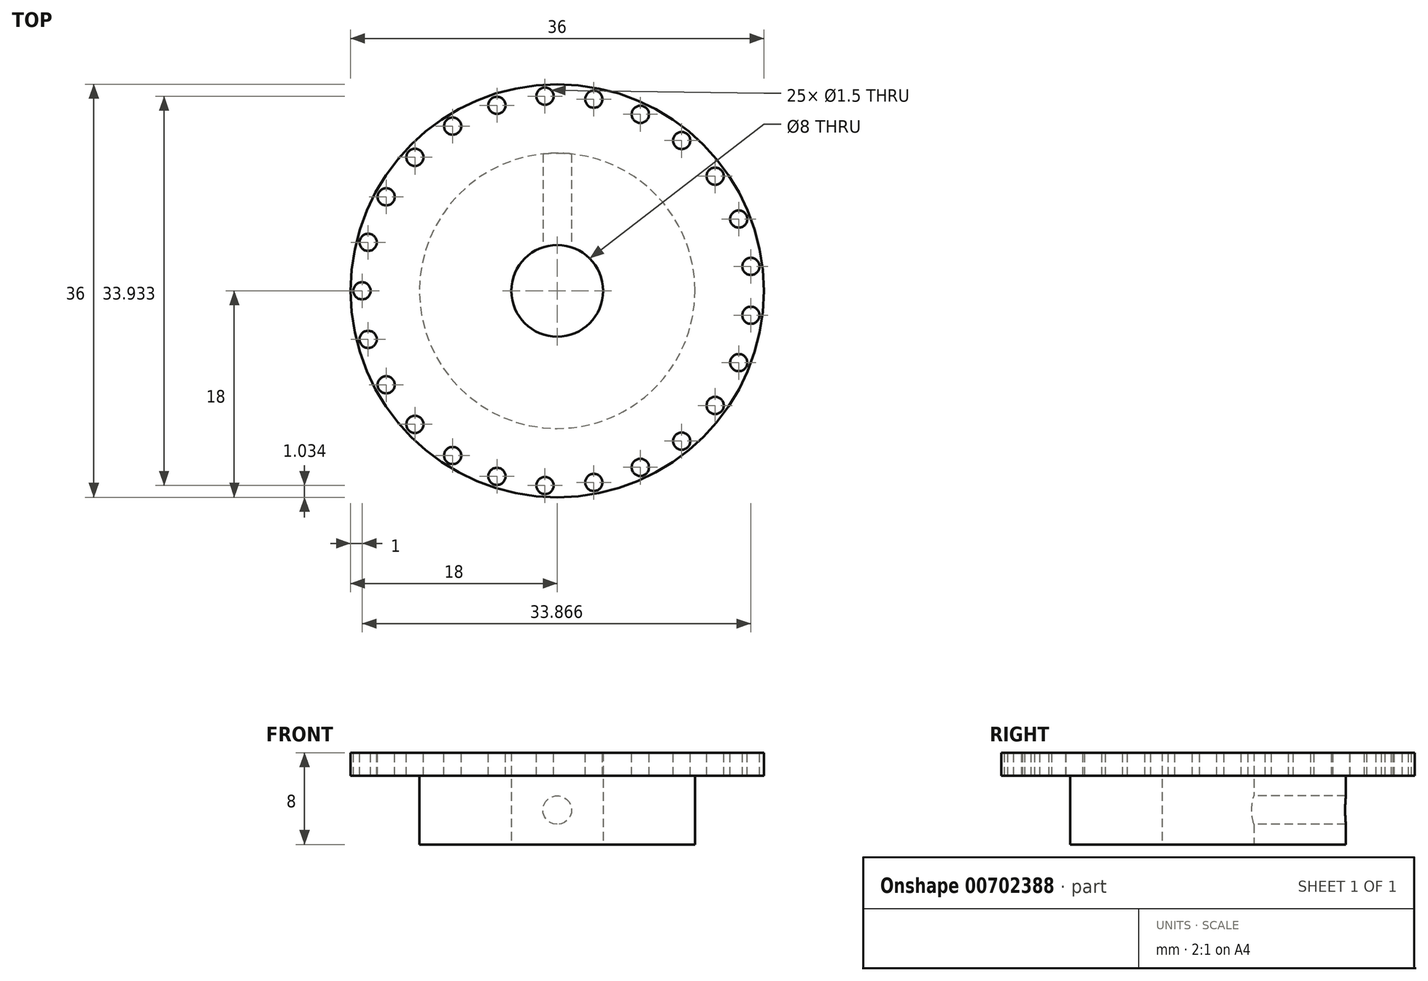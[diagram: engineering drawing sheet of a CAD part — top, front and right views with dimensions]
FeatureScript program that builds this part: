
annotation { "Feature Type Name" : "Feature", "Feature Type Description" : "" }
export const myFeature = defineFeature(function(context is Context, id is Id, definition is map)
    precondition{}
    {
        {
            var Q0;
            Q0=qCreatedBy(makeId("Top.planeOp"),FACE);
            var sketch = newSketch(context, id + "F0", { "sketchPlane" : qUnion([Q0])});
            skCircle(sketch, "E0", {"center": v(0, 0) * mm, "radius": 12 * mm});
            skSolve(sketch);
        }
        {
            var Q0;
            Q0 = qSketchRegion(id + "F0", true);
            extrude(context, id + "F1", {"entities" : qUnion([Q0]), "depth" : 6 * mm, "offsetDistance" : 25 * mm});
        }
        {
            var Q0;
            Q0=makeQuery(id+"F1.opExtrude","CAP_FACE",FACE,{"disambiguationData":[OSD([sQuery(id+"F0.wireOp",EDGE,"E0")])],"isStart":false});
            var sketch = newSketch(context, id + "F2", { "sketchPlane" : qUnion([Q0])});
            skCircle(sketch, "E1", {"center": v(0, 0) * mm, "radius": 18 * mm});
            skSolve(sketch);
        }
        {
            var Q0;
            Q0 = qSketchRegion(id + "F2", true);
            extrude(context, id + "F3", {"entities" : qUnion([Q0]), "operationType" : NewBodyOperationType.ADD, "depth" : 2 * mm, "offsetDistance" : 25 * mm});
        }
        {
            var Q0;
            Q0=makeQuery(id+"F3.opExtrude","CAP_FACE",FACE,{"disambiguationData":[OSD([sQuery(id+"F2.wireOp",EDGE,"E1")])],"isStart":false});
            var sketch = newSketch(context, id + "F4", { "sketchPlane" : qUnion([Q0])});
            skCircle(sketch, "E2", {"center": v(0, 0) * mm, "radius": 18 * mm});
            skCircle(sketch, "E3.0", {"center": v(0, 0) * mm, "radius": 17 * mm});
            skCircle(sketch, "E4", {"center": v(-17, 0) * mm, "radius": 0.75 * mm});
            skCircle(sketch, "E5.1.0", {"center": v(-16.47, -4.23) * mm, "radius": 0.75 * mm});
            skCircle(sketch, "E5.2.0", {"center": v(-14.9, -8.19) * mm, "radius": 0.75 * mm});
            skCircle(sketch, "E5.3.0", {"center": v(-12.4, -11.64) * mm, "radius": 0.75 * mm});
            skCircle(sketch, "E5.4.0", {"center": v(-9.1, -14.35) * mm, "radius": 0.75 * mm});
            skCircle(sketch, "E5.5.0", {"center": v(-5.25, -16.17) * mm, "radius": 0.75 * mm});
            skCircle(sketch, "E5.6.0", {"center": v(-1.07, -16.97) * mm, "radius": 0.75 * mm});
            skCircle(sketch, "E5.7.0", {"center": v(3.19, -16.7) * mm, "radius": 0.75 * mm});
            skCircle(sketch, "E5.8.0", {"center": v(7.24, -15.38) * mm, "radius": 0.75 * mm});
            skCircle(sketch, "E5.9.0", {"center": v(10.84, -13.1) * mm, "radius": 0.75 * mm});
            skCircle(sketch, "E5.10.0", {"center": v(13.75, -10) * mm, "radius": 0.75 * mm});
            skCircle(sketch, "E5.11.0", {"center": v(15.8, -6.26) * mm, "radius": 0.75 * mm});
            skCircle(sketch, "E5.12.0", {"center": v(16.87, -2.13) * mm, "radius": 0.75 * mm});
            skCircle(sketch, "E5.13.0", {"center": v(16.87, 2.13) * mm, "radius": 0.75 * mm});
            skCircle(sketch, "E5.14.0", {"center": v(15.8, 6.26) * mm, "radius": 0.75 * mm});
            skCircle(sketch, "E5.15.0", {"center": v(13.75, 10) * mm, "radius": 0.75 * mm});
            skCircle(sketch, "E5.16.0", {"center": v(10.84, 13.1) * mm, "radius": 0.75 * mm});
            skCircle(sketch, "E5.17.0", {"center": v(7.24, 15.38) * mm, "radius": 0.75 * mm});
            skCircle(sketch, "E5.18.0", {"center": v(3.19, 16.7) * mm, "radius": 0.75 * mm});
            skCircle(sketch, "E5.19.0", {"center": v(-1.07, 16.97) * mm, "radius": 0.75 * mm});
            skCircle(sketch, "E5.20.0", {"center": v(-5.25, 16.17) * mm, "radius": 0.75 * mm});
            skCircle(sketch, "E5.21.0", {"center": v(-9.1, 14.35) * mm, "radius": 0.75 * mm});
            skCircle(sketch, "E5.22.0", {"center": v(-12.4, 11.64) * mm, "radius": 0.75 * mm});
            skCircle(sketch, "E5.23.0", {"center": v(-14.9, 8.19) * mm, "radius": 0.75 * mm});
            skCircle(sketch, "E5.24.0", {"center": v(-16.47, 4.23) * mm, "radius": 0.75 * mm});
            skSolve(sketch);
        }
        {
            var Q0;
            Q0=sQuery(id+"F4.wireOp",VERTEX,"E4.center");
            var Q1;
            Q1=sQuery(id+"F4.wireOp",VERTEX,"E5.24.0.center");
            var Q2;
            Q2=sQuery(id+"F4.wireOp",VERTEX,"E5.23.0.center");
            var Q3;
            Q3=sQuery(id+"F4.wireOp",VERTEX,"E5.22.0.center");
            var Q4;
            Q4=sQuery(id+"F4.wireOp",VERTEX,"E5.21.0.center");
            var Q5;
            Q5=sQuery(id+"F4.wireOp",VERTEX,"E5.20.0.center");
            var Q6;
            Q6=sQuery(id+"F4.wireOp",VERTEX,"E5.19.0.center");
            var Q7;
            Q7=sQuery(id+"F4.wireOp",VERTEX,"E5.18.0.center");
            var Q8;
            Q8=sQuery(id+"F4.wireOp",VERTEX,"E5.17.0.center");
            var Q9;
            Q9=sQuery(id+"F4.wireOp",VERTEX,"E5.16.0.center");
            var Q10;
            Q10=sQuery(id+"F4.wireOp",VERTEX,"E5.15.0.center");
            var Q11;
            Q11=sQuery(id+"F4.wireOp",VERTEX,"E5.14.0.center");
            var Q12;
            Q12=sQuery(id+"F4.wireOp",VERTEX,"E5.1.0.center");
            var Q13;
            Q13=sQuery(id+"F4.wireOp",VERTEX,"E5.2.0.center");
            var Q14;
            Q14=sQuery(id+"F4.wireOp",VERTEX,"E5.3.0.center");
            var Q15;
            Q15=sQuery(id+"F4.wireOp",VERTEX,"E5.4.0.center");
            var Q16;
            Q16=sQuery(id+"F4.wireOp",VERTEX,"E5.5.0.center");
            var Q17;
            Q17=sQuery(id+"F4.wireOp",VERTEX,"E5.6.0.center");
            var Q18;
            Q18=sQuery(id+"F4.wireOp",VERTEX,"E5.7.0.center");
            var Q19;
            Q19=sQuery(id+"F4.wireOp",VERTEX,"E5.8.0.center");
            var Q20;
            Q20=sQuery(id+"F4.wireOp",VERTEX,"E5.9.0.center");
            var Q21;
            Q21=sQuery(id+"F4.wireOp",VERTEX,"E5.10.0.center");
            var Q22;
            Q22=sQuery(id+"F4.wireOp",VERTEX,"E5.11.0.center");
            var Q23;
            Q23=sQuery(id+"F4.wireOp",VERTEX,"E5.12.0.center");
            var Q24;
            Q24=sQuery(id+"F4.wireOp",VERTEX,"E5.13.0.center");
            var Q25;
            Q25=makeQuery(id+"F1.opExtrude","SWEPT_BODY",BODY,{"disambiguationData":[OSD([sQuery(id+"F0.wireOp",EDGE,"E0")])]});
            hole(context, id + "F5", {"style" : HoleStyle.SIMPLE, "endStyle" : HoleEndStyle.THROUGH, "holeDiameter" : 1.5 * mm, "majorDiameter" : 5 * mm, "isTappedThrough" : true, "tappedDepth" : 12 * mm, "tapClearance" : 3, "locations" : qUnion([Q0, Q1, Q2, Q3, Q4, Q5, Q6, Q7, Q8, Q9, Q10, Q11, Q12, Q13, Q14, Q15, Q16, Q17, Q18, Q19, Q20, Q21, Q22, Q23, Q24]), "scope" : qUnion([Q25])});
        }
        {
            var Q0;
            Q0=makeQuery(id+"F1.opExtrude","CAP_FACE",FACE,{"disambiguationData":[OSD([sQuery(id+"F0.wireOp",EDGE,"E0")])],"isStart":true});
            var sketch = newSketch(context, id + "F6", { "sketchPlane" : qUnion([Q0])});
            skCircle(sketch, "E6", {"center": v(0, 0) * mm, "radius": 4 * mm});
            skSolve(sketch);
        }
        {
            var Q0;
            Q0 = qSketchRegion(id + "F6", true);
            extrude(context, id + "F7", {"entities" : qUnion([Q0]), "operationType" : NewBodyOperationType.REMOVE, "endBound" : BoundingType.THROUGH_ALL, "oppositeDirection" : true, "depth" : 25 * mm, "offsetDistance" : 25 * mm});
        }
        {
            var Q0;
            Q0=qCreatedBy(makeId("Front.planeOp"),FACE);
            var sketch = newSketch(context, id + "F8", { "sketchPlane" : qUnion([Q0])});
            skLineSegment(sketch, "E7", {"start": v(0, 0) * mm, "end": v(0, 11.38) * mm});
            skLineSegment(sketch, "E8", {"start": v(-13.15, 0) * mm, "end": v(15.67, 0) * mm});
            skLineSegment(sketch, "E9.0", {"start": v(-13.15, 3) * mm, "end": v(15.67, 3) * mm});
            skCircle(sketch, "E10", {"center": v(0, 3) * mm, "radius": 1.55 * mm});
            skSolve(sketch);
        }
        {
            var Q0;
            Q0=sQuery(id+"F8.wireOp",VERTEX,"E10.center");
            var Q1;
            Q1=makeQuery(id+"F1.opExtrude","SWEPT_BODY",BODY,{"disambiguationData":[OSD([sQuery(id+"F0.wireOp",EDGE,"E0")])]});
            hole(context, id + "F9", {"style" : HoleStyle.SIMPLE, "endStyle" : HoleEndStyle.THROUGH, "standardTappedOrClearance" : lookupTablePath({ "standard" : "ISO", "engagement" : "75%", "pitch" : "0.5 mm", "size" : "M3", "type" : "Tapped" }), "standardBlindInLast" : lookupTablePath({ "standard" : "ISO", "engagement" : "75%", "pitch" : "0.5 mm", "size" : "M3", "type" : "Tapped" }), "holeDiameter" : 2.5 * mm, "majorDiameter" : 3 * mm, "showTappedDepth" : true, "isTappedThrough" : true, "tappedDepth" : 12 * mm, "tapClearance" : 3, "locations" : qUnion([Q0]), "scope" : qUnion([Q1])});
        }
    });
